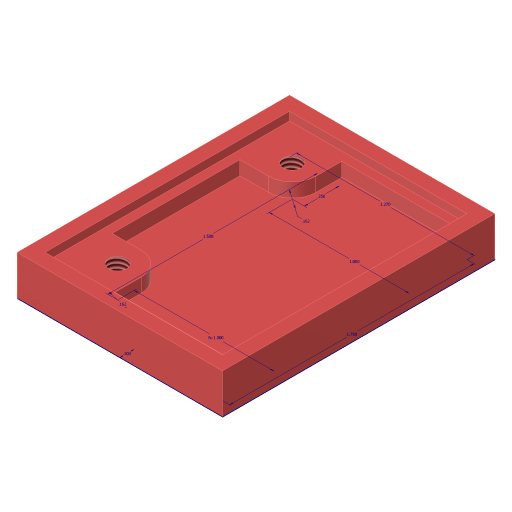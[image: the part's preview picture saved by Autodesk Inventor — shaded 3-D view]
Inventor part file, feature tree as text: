
AUTODESK INVENTOR PART (.ipt)
format: ipt  version: 2023.4 (Build 274418000, 418)  size: 153,088 bytes
history: native  units: in
note: dims shown in document units (in); Inventor stores cm internally (conversion verified against a paired STEP export)
features: sketch x3, extrude x3, hole x1, projected_geometry x1
ambient origin geometry x8: Origin, YZ Plane, XZ Plane, XY Plane, X Axis, Y Axis, Z Axis, Center Point
bodies: Solid1 (feature_tree)
feature tree (8):
  sketch  "Sketch2"  dims[d0=1.27in d1=1.75in]
  extrude  "Extrusion1"  Depth=1.75in
  extrude  "Extrusion2"  Depth=0.125in TaperAngle=0.0deg
  sketch  "Sketch5"  dims[d2=0.1in d3=0.125in d4=0.0in]
  extrude  "Extrusion4"  Depth=0.0625in
  hole  "Hole2"  [1 undecoded]
  sketch  "Sketch6"  dims[d5=0.285in d6=0.0in d23=0.0625in d24=0.0625in d25=0.0625in d26=0.1in d27=0.0in d29=0.375in d31=0.375in d32=1.0in d33=1.0in d34=0.25in d35=1.5in d36=0.13in d37=0.328in d38=0.375in d39=0.25in d40=0.5635in d41=1.0in d42=0.8108in d43=0.162in d44=0.162in]
  projected_geometry  "Projected Loop2"
note: 1 required parameter value undecoded (feature->parameter linkage not recoverable at this tier; creation-order binding heuristic only, values carry confidence <= 0.55)
